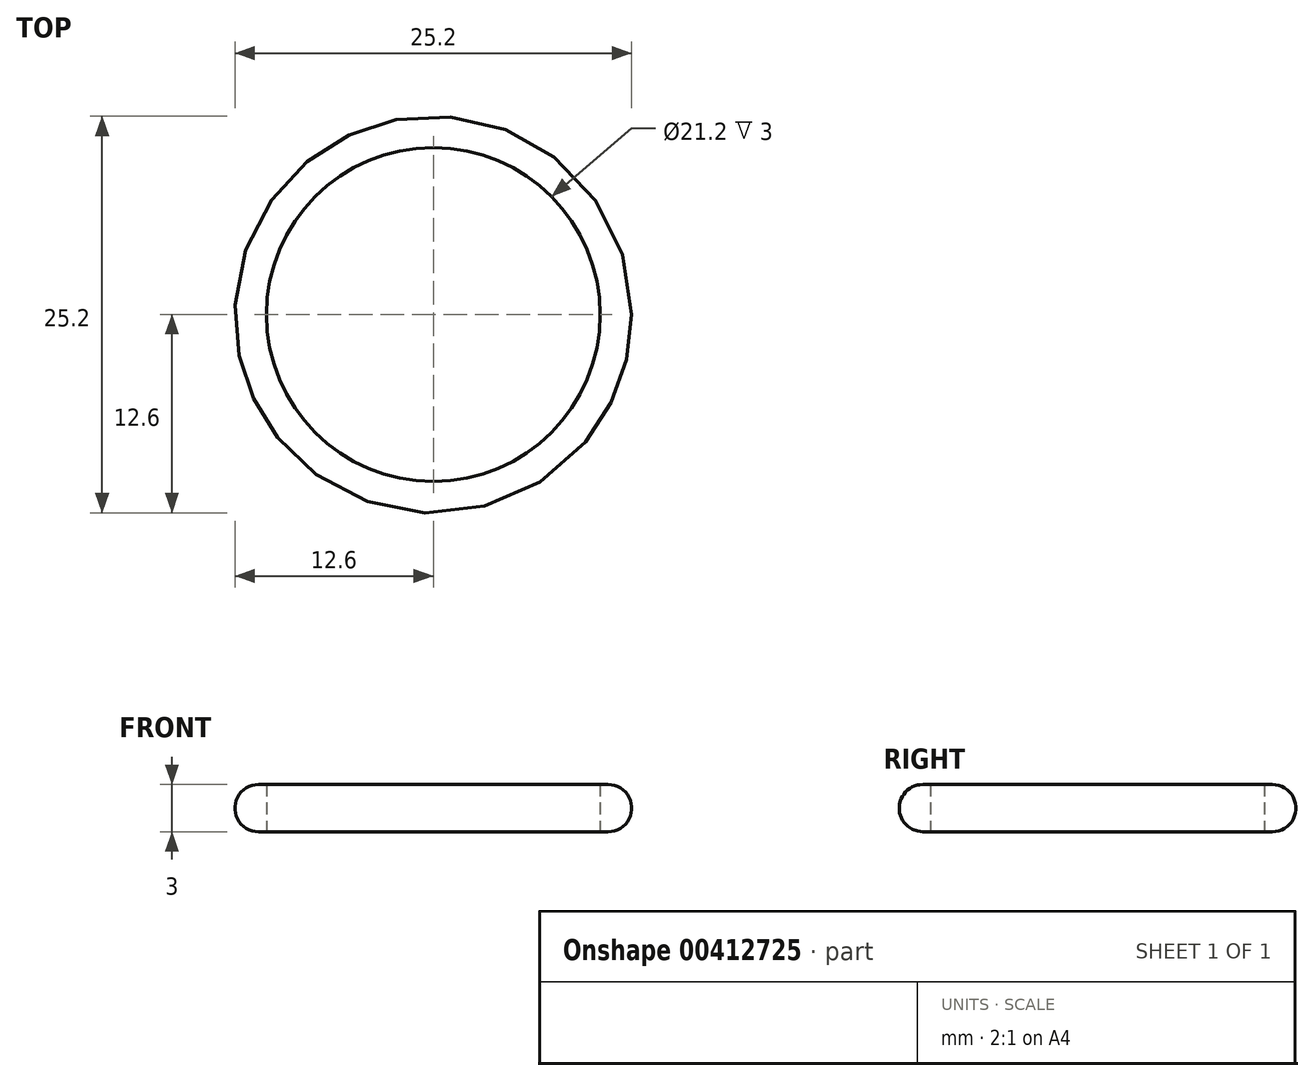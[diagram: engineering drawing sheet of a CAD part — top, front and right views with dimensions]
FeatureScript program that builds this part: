
annotation { "Feature Type Name" : "Feature", "Feature Type Description" : "" }
export const myFeature = defineFeature(function(context is Context, id is Id, definition is map)
    precondition{}
    {
        {
            var Q0;
            Q0=qCreatedBy(makeId("Top.planeOp"),FACE);
            var sketch = newSketch(context, id + "F0", { "sketchPlane" : qUnion([Q0]), "disableImprinting" : false});
            skCircle(sketch, "E0", {"center": v(0, 0) * mm, "radius": 10.6 * mm});
            skCircle(sketch, "E1", {"center": v(0, 0) * mm, "radius": 12.6 * mm});
            skSolve(sketch);
        }
        {
            var Q0;
            Q0=makeQuery(id+"F0.imprint","IMPRINT",FACE,{"disambiguationData":[TD([[makeQuery(id+"F0.imprint","IMPRINT",EDGE,{"derivedFrom":sQuery(id+"F0.wireOp",EDGE,"E0")}),-1.0]])]});
            extrude(context, id + "F1", {"entities" : qUnion([Q0]), "depth" : 3 * mm, "offsetDistance" : 25 * mm});
        }
        {
            var Q0;
            Q0=makeQuery(id+"F1.opExtrude","CAP_EDGE",EDGE,{"disambiguationData":[OSD([sQuery(id+"F0.wireOp",EDGE,"E1")])],"isStart":false});
            var Q1;
            Q1=makeQuery(id+"F1.opExtrude","CAP_EDGE",EDGE,{"disambiguationData":[OSD([sQuery(id+"F0.wireOp",EDGE,"E1")])],"isStart":true});
            fillet(context, id + "F2", {"entities" : qUnion([Q0, Q1]), "radius" : 1.5 * mm, "tangentPropagation" : true, "allowEdgeOverflow" : false});
        }
    });
